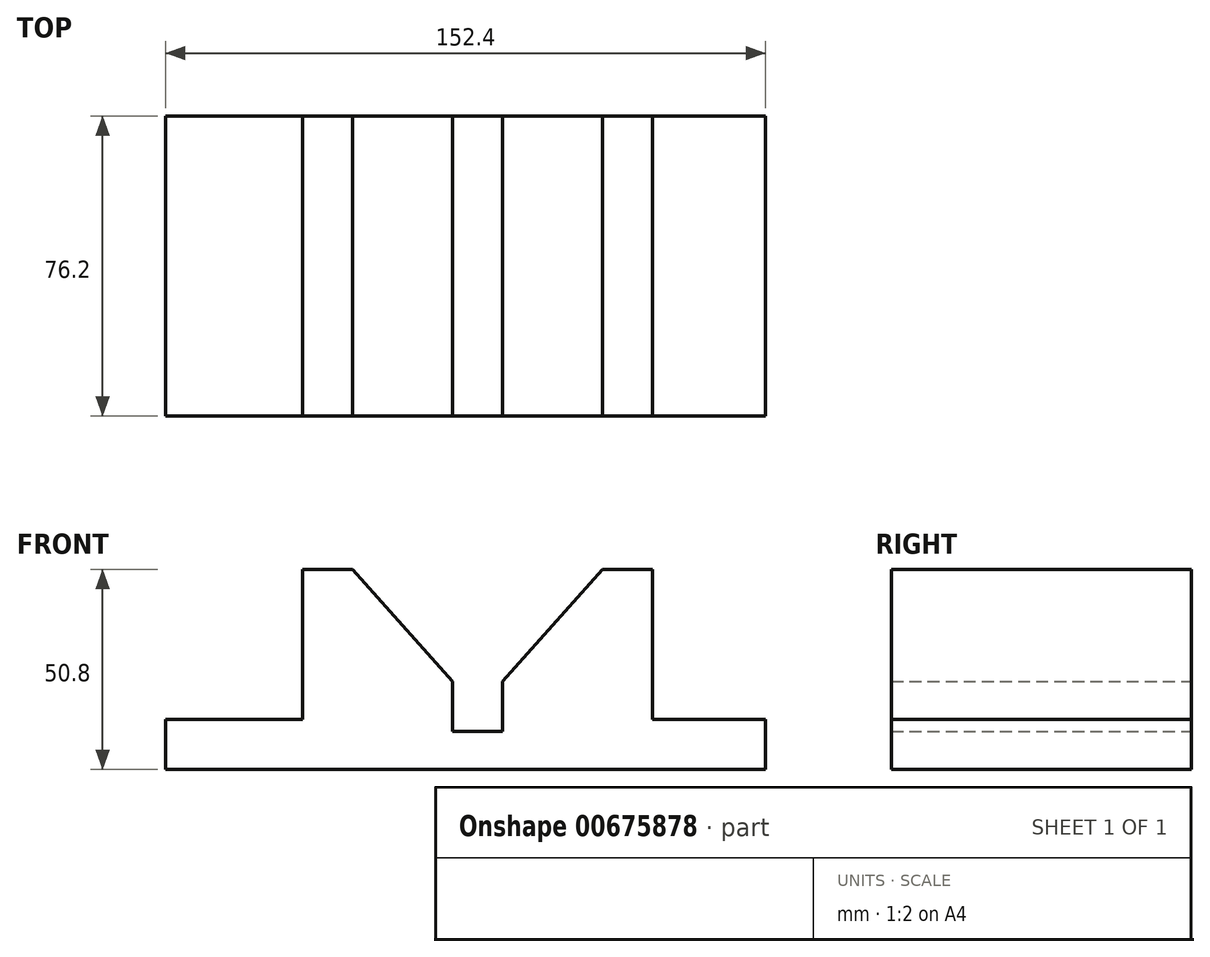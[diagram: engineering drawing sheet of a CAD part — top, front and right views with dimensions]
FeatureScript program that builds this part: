
annotation { "Feature Type Name" : "Feature", "Feature Type Description" : "" }
export const myFeature = defineFeature(function(context is Context, id is Id, definition is map)
    precondition{}
    {
        {
            var Q0;
            Q0=qCreatedBy(makeId("Front.planeOp"),FACE);
            var sketch = newSketch(context, id + "F0", { "sketchPlane" : qUnion([Q0])});
            skLineSegment(sketch, "E0", {"start": v(-72.17, -23.32) * mm, "end": v(80.23, -23.32) * mm});
            skLineSegment(sketch, "E1", {"start": v(80.23, -23.32) * mm, "end": v(80.23, -10.62) * mm});
            skLineSegment(sketch, "E2", {"start": v(80.23, -10.62) * mm, "end": v(51.47, -10.62) * mm});
            skLineSegment(sketch, "E3", {"start": v(51.47, -10.62) * mm, "end": v(51.47, 27.48) * mm});
            skLineSegment(sketch, "E4", {"start": v(51.47, 27.48) * mm, "end": v(38.77, 27.48) * mm});
            skLineSegment(sketch, "E5", {"start": v(38.77, 27.48) * mm, "end": v(13.37, -0.92) * mm});
            skLineSegment(sketch, "E6", {"start": v(0.67, -0.92) * mm, "end": v(-24.73, 27.48) * mm});
            skLineSegment(sketch, "E7", {"start": v(-24.73, 27.48) * mm, "end": v(-37.43, 27.48) * mm});
            skLineSegment(sketch, "E8", {"start": v(-37.43, 27.48) * mm, "end": v(-37.43, -10.62) * mm});
            skLineSegment(sketch, "E9", {"start": v(-37.43, -10.62) * mm, "end": v(-72.17, -10.62) * mm});
            skLineSegment(sketch, "E10", {"start": v(-72.17, -10.62) * mm, "end": v(-72.17, -23.32) * mm});
            skLineSegment(sketch, "E11", {"start": v(13.37, -0.92) * mm, "end": v(13.37, -13.62) * mm});
            skLineSegment(sketch, "E12", {"start": v(13.37, -13.62) * mm, "end": v(0.67, -13.62) * mm});
            skLineSegment(sketch, "E13", {"start": v(0.67, -13.62) * mm, "end": v(0.67, -0.92) * mm});
            skSolve(sketch);
        }
        {
            var Q0;
            Q0 = qSketchRegion(id + "F0", true);
            extrude(context, id + "F1", {"entities" : qUnion([Q0]), "depth" : 76.2 * mm, "offsetDistance" : 25.4 * mm});
        }
    });
